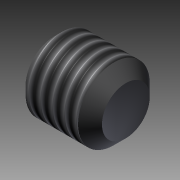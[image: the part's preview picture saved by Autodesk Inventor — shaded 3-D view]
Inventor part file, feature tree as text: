
AUTODESK INVENTOR PART (.ipt)
format: ipt  version: 2011 SP1 (Build 150282100, 282)  size: 114,176 bytes
history: native  units: mm
features: other x7, sketch x3, revolve x2, thread x1, extrude x1
ambient origin geometry x8: Origin, YZ Plane, XZ Plane, XY Plane, X Axis, Y Axis, Z Axis, Center Point
bodies: Solid1 (feature_tree)
feature tree (14):
  revolve  "Revolution1"  [1 undecoded]
  thread  "Thread1"  [1 undecoded]
  extrude  "Extrusion1"  TaperAngle=0.0deg  [1 undecoded]
  revolve  "Revolution2"  [1 undecoded]
  other  "CP_XY"
  other  "CP_YZ"
  other  "CP_ZX"
  other  "CP_X"
  other  "CP_Y"
  other  "CP_Z"
  other  "CP_Center"
  sketch  "Sketch_1"  dims[d0=360.0deg d1=2.1935mm d2=0.0mm d3=1.2mm d4=0.0mm]
  sketch  "Sketch_2"  dims[d5=360.0deg d6=0.0mm]
  sketch  "Sketch_3"
note: 4 required parameter values undecoded (feature->parameter linkage not recoverable at this tier; creation-order binding heuristic only, values carry confidence <= 0.55)